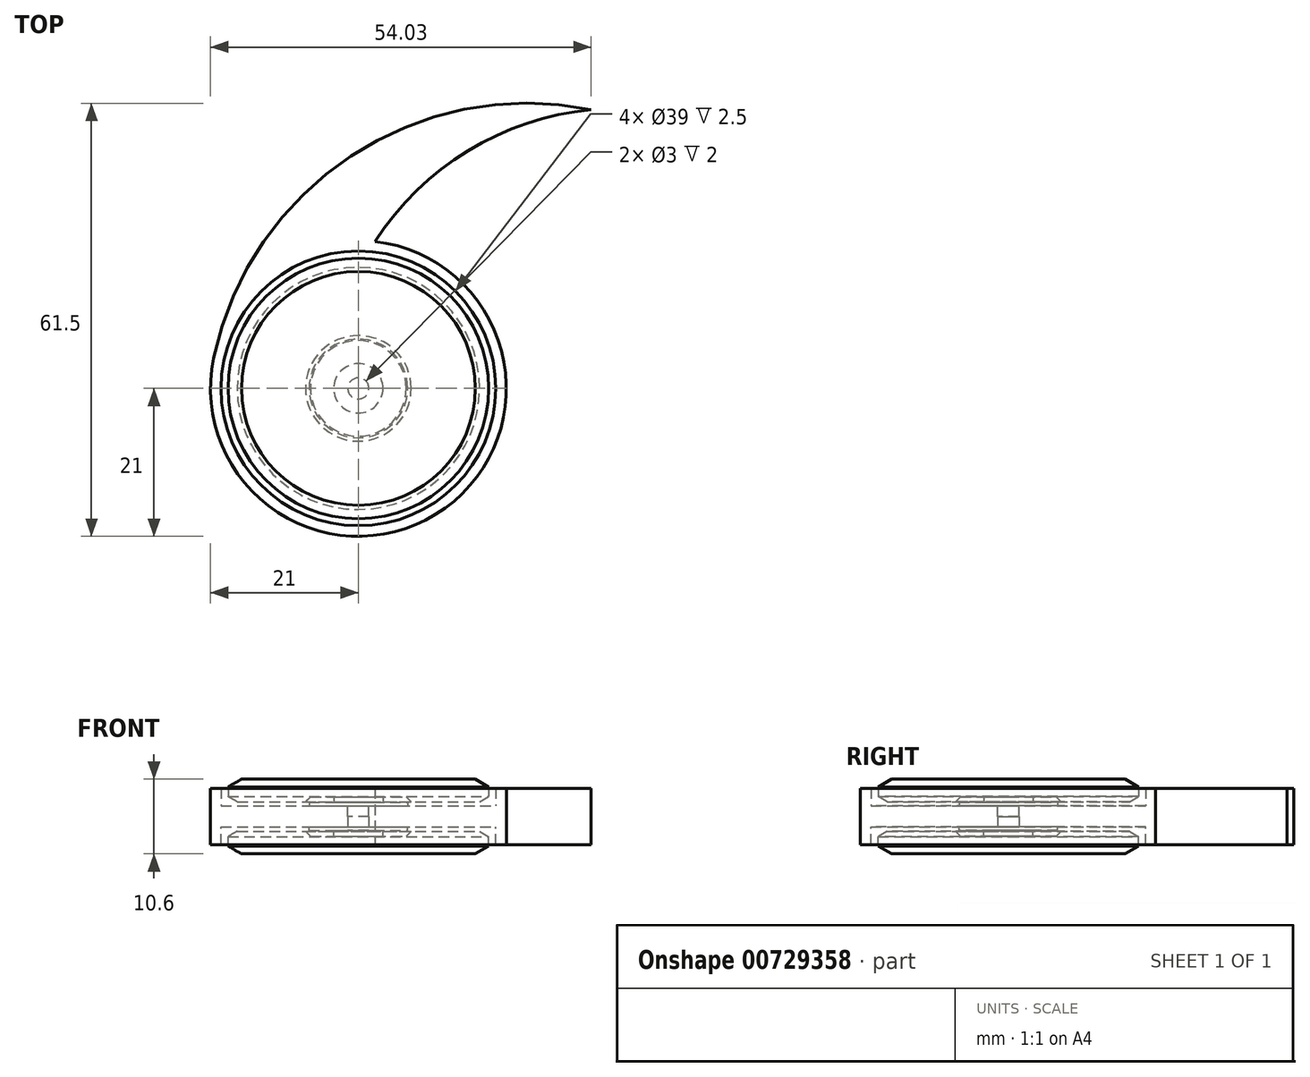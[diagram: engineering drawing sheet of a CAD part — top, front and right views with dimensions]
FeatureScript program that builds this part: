
annotation { "Feature Type Name" : "Feature", "Feature Type Description" : "" }
export const myFeature = defineFeature(function(context is Context, id is Id, definition is map)
    precondition{}
    {
        {
            var Q0;
            Q0=qCreatedBy(makeId("Top.planeOp"),FACE);
            var sketch = newSketch(context, id + "F0", { "sketchPlane" : qUnion([Q0])});
            skCircle(sketch, "E0", {"center": v(0, 0) * mm, "radius": 5 * mm});
            skCircle(sketch, "E1", {"center": v(0, 0) * mm, "radius": 1.5 * mm});
            skSolve(sketch);
        }
        {
            var Q0;
            Q0=qSketchRegion(id+"F0",true);
            extrude(context, id + "F1", {"entities" : qUnion([Q0]), "depth" : 2 * mm, "offsetDistance" : 25 * mm});
        }
        {
            var Q0;
            Q0=qCreatedBy(makeId("Front.planeOp"),FACE);
            var sketch = newSketch(context, id + "F2", { "sketchPlane" : qUnion([Q0])});
            skLineSegment(sketch, "E2", {"start": v(-5, 0) * mm, "end": v(-5, 2) * mm});
            skLineSegment(sketch, "E3", {"start": v(-5, 0) * mm, "end": v(-21, 0) * mm});
            skLineSegment(sketch, "E4", {"start": v(-21, 0) * mm, "end": v(-21, 4) * mm});
            skLineSegment(sketch, "E5", {"start": v(-21, 4) * mm, "end": v(-19.5, 4) * mm});
            skLineSegment(sketch, "E6", {"start": v(-19.5, 4) * mm, "end": v(-19.5, 1.5) * mm});
            skLineSegment(sketch, "E7", {"start": v(-19.5, 1.5) * mm, "end": v(-7, 1.5) * mm});
            skLineSegment(sketch, "E8", {"start": v(-7, 1.5) * mm, "end": v(-7, 2) * mm});
            skLineSegment(sketch, "E9", {"start": v(-7, 2) * mm, "end": v(-5, 2) * mm});
            skLineSegment(sketch, "E10", {"start": v(0, 0) * mm, "end": v(0, 5.83) * mm, "construction": true});
            skLineSegment(sketch, "E11.0", {"start": v(-5, 2) * mm, "end": v(5, 2) * mm, "construction": true});
            skSolve(sketch);
        }
        {
            var Q0;
            Q0=qSketchRegion(id+"F2",true);
            var Q1;
            Q1=sQuery(id+"F2.wireOp",EDGE,"E10");
            revolve(context, id + "F3", {"surfaceOperationType" : NewSurfaceOperationType.NEW, "entities" : qUnion([Q0]), "axis" : qUnion([Q1]), "revolveType" : RevolveType.FULL});
        }
        {
            var Q0;
            Q0=qCreatedBy(makeId("Front.planeOp"),FACE);
            var sketch = newSketch(context, id + "F4", { "sketchPlane" : qUnion([Q0])});
            skLineSegment(sketch, "E12", {"start": v(0, 5.3) * mm, "end": v(-16.6, 5.3) * mm});
            skLineSegment(sketch, "E13", {"start": v(-16.6, 5.3) * mm, "end": v(-18.5, 4.2) * mm});
            skLineSegment(sketch, "E14", {"start": v(-18.5, 4.2) * mm, "end": v(-18.5, 2.84) * mm});
            skLineSegment(sketch, "E15", {"start": v(-18.5, 2.84) * mm, "end": v(-17.2, 2.1) * mm});
            skLineSegment(sketch, "E16", {"start": v(-17.2, 2.1) * mm, "end": v(-7.5, 2.1) * mm});
            skLineSegment(sketch, "E17", {"start": v(-18.5, 3.52) * mm, "end": v(-15.02, 3.52) * mm, "construction": true});
            skLineSegment(sketch, "E18", {"start": v(19.5, 4) * mm, "end": v(19.5, 1.5) * mm});
            skLineSegment(sketch, "E19", {"start": v(-19.5, 1.5) * mm, "end": v(-19.5, 4) * mm});
            skLineSegment(sketch, "E20.0.0", {"start": v(-5, 2) * mm, "end": v(5, 2) * mm});
            skLineSegment(sketch, "E21", {"start": v(-7.5, 2.1) * mm, "end": v(-6.8, 2.8) * mm});
            skLineSegment(sketch, "E22", {"start": v(-7.5, 2.1) * mm, "end": v(-6.48, 2.1) * mm, "construction": true});
            skLineSegment(sketch, "E23", {"start": v(-6.8, 2.8) * mm, "end": v(-3.5, 2.8) * mm});
            skLineSegment(sketch, "E24", {"start": v(-3.5, 2.8) * mm, "end": v(-3.5, 2) * mm});
            skLineSegment(sketch, "E25", {"start": v(-1.5, 0) * mm, "end": v(0, 0) * mm});
            skLineSegment(sketch, "E26", {"start": v(0, 0) * mm, "end": v(0, 5.3) * mm});
            skLineSegment(sketch, "E27", {"start": v(-1.5, 0) * mm, "end": v(-1.5, 2) * mm});
            skLineSegment(sketch, "E28.0", {"start": v(21, 4) * mm, "end": v(-21, 4) * mm, "construction": true});
            skSolve(sketch);
        }
        {
            var Q0;
            Q0=qSketchRegion(id+"F4",true);
            var Q1;
            Q1=sQuery(id+"F4.wireOp",EDGE,"E26");
            revolve(context, id + "F5", {"surfaceOperationType" : NewSurfaceOperationType.NEW, "entities" : qUnion([Q0]), "axis" : qUnion([Q1]), "revolveType" : RevolveType.FULL});
        }
        {
            var Q0;
            Q0=qCreatedBy(makeId("Top.planeOp"),FACE);
            var sketch = newSketch(context, id + "F6", { "sketchPlane" : qUnion([Q0])});
            skCircle(sketch, "E29", {"center": v(23.98, -5) * mm, "radius": 45.5 * mm});
            skCircle(sketch, "E30.0", {"center": v(0, 0) * mm, "radius": 21 * mm});
            skArc(sketch, "E31", {"start": v(33.03, 39.6) * mm, "mid": v(15.56, 33.73) * mm, "end": v(2.38, 20.86) * mm});
            skSolve(sketch);
        }
        {
            var Q0;
            {var subQ0=sQuery(id+"F6.wireOp",EDGE,"E31");Q0=makeQuery(id+"F6.imprint","IMPRINT",FACE,{"disambiguationData":[TD([[makeQuery(id+"F6.imprint","IMPRINT",EDGE,{"derivedFrom":subQ0}),-1.0]])]});}
            var Q1;
            Q1=makeQuery(id+"F3.opRevolve","SWEPT_FACE",FACE,{"disambiguationData":[OSD([sQuery(id+"F2.wireOp",EDGE,"E5")])]});
            extrude(context, id + "F7", {"entities" : qUnion([Q0]), "operationType" : NewBodyOperationType.ADD, "endBound" : BoundingType.UP_TO_SURFACE, "depth" : 25 * mm, "endBoundEntityFace" : qUnion([Q1]), "offsetDistance" : 25 * mm});
        }
        {
            var Q0;
            Q0=makeQuery(id+"F3.opRevolve","SWEPT_BODY",BODY,{"disambiguationData":[OSD([sQuery(id+"F2.wireOp",EDGE,"E2"),sQuery(id+"F2.wireOp",EDGE,"E3"),sQuery(id+"F2.wireOp",EDGE,"E4"),sQuery(id+"F2.wireOp",EDGE,"E5"),sQuery(id+"F2.wireOp",EDGE,"E6"),sQuery(id+"F2.wireOp",EDGE,"E7"),sQuery(id+"F2.wireOp",EDGE,"E8"),sQuery(id+"F2.wireOp",EDGE,"E9")])]});
            var Q1;
            Q1=qCreatedBy(makeId("Top.planeOp"),FACE);
            mirror(context, id + "F8", {"operationType" : NewBodyOperationType.ADD, "entities" : qUnion([Q0]), "mirrorPlane" : qUnion([Q1])});
        }
        {
            var Q0;
            Q0=makeQuery(id+"F1.opExtrude","SWEPT_BODY",BODY,{"disambiguationData":[OSD([sQuery(id+"F0.wireOp",EDGE,"E0"),sQuery(id+"F0.wireOp",EDGE,"E1")])]});
            var Q1;
            Q1=qCreatedBy(makeId("Top.planeOp"),FACE);
            mirror(context, id + "F10", {"operationType" : NewBodyOperationType.ADD, "entities" : qUnion([Q0]), "mirrorPlane" : qUnion([Q1])});
        }
        {
            var Q0;
            Q0=makeQuery(id+"F5.opRevolve","SWEPT_BODY",BODY,{"disambiguationData":[OSD([sQuery(id+"F4.wireOp",EDGE,"E12"),sQuery(id+"F4.wireOp",EDGE,"E13"),sQuery(id+"F4.wireOp",EDGE,"E14"),sQuery(id+"F4.wireOp",EDGE,"E15"),sQuery(id+"F4.wireOp",EDGE,"E16"),sQuery(id+"F4.wireOp",EDGE,"E20.0.0"),sQuery(id+"F4.wireOp",EDGE,"E21"),sQuery(id+"F4.wireOp",EDGE,"E23"),sQuery(id+"F4.wireOp",EDGE,"E24"),sQuery(id+"F4.wireOp",EDGE,"E25"),sQuery(id+"F4.wireOp",EDGE,"E26"),sQuery(id+"F4.wireOp",EDGE,"E27")])]});
            var Q1;
            Q1=qCreatedBy(makeId("Top.planeOp"),FACE);
            mirror(context, id + "F11", {"entities" : qUnion([Q0]), "mirrorPlane" : qUnion([Q1])});
        }
    });
